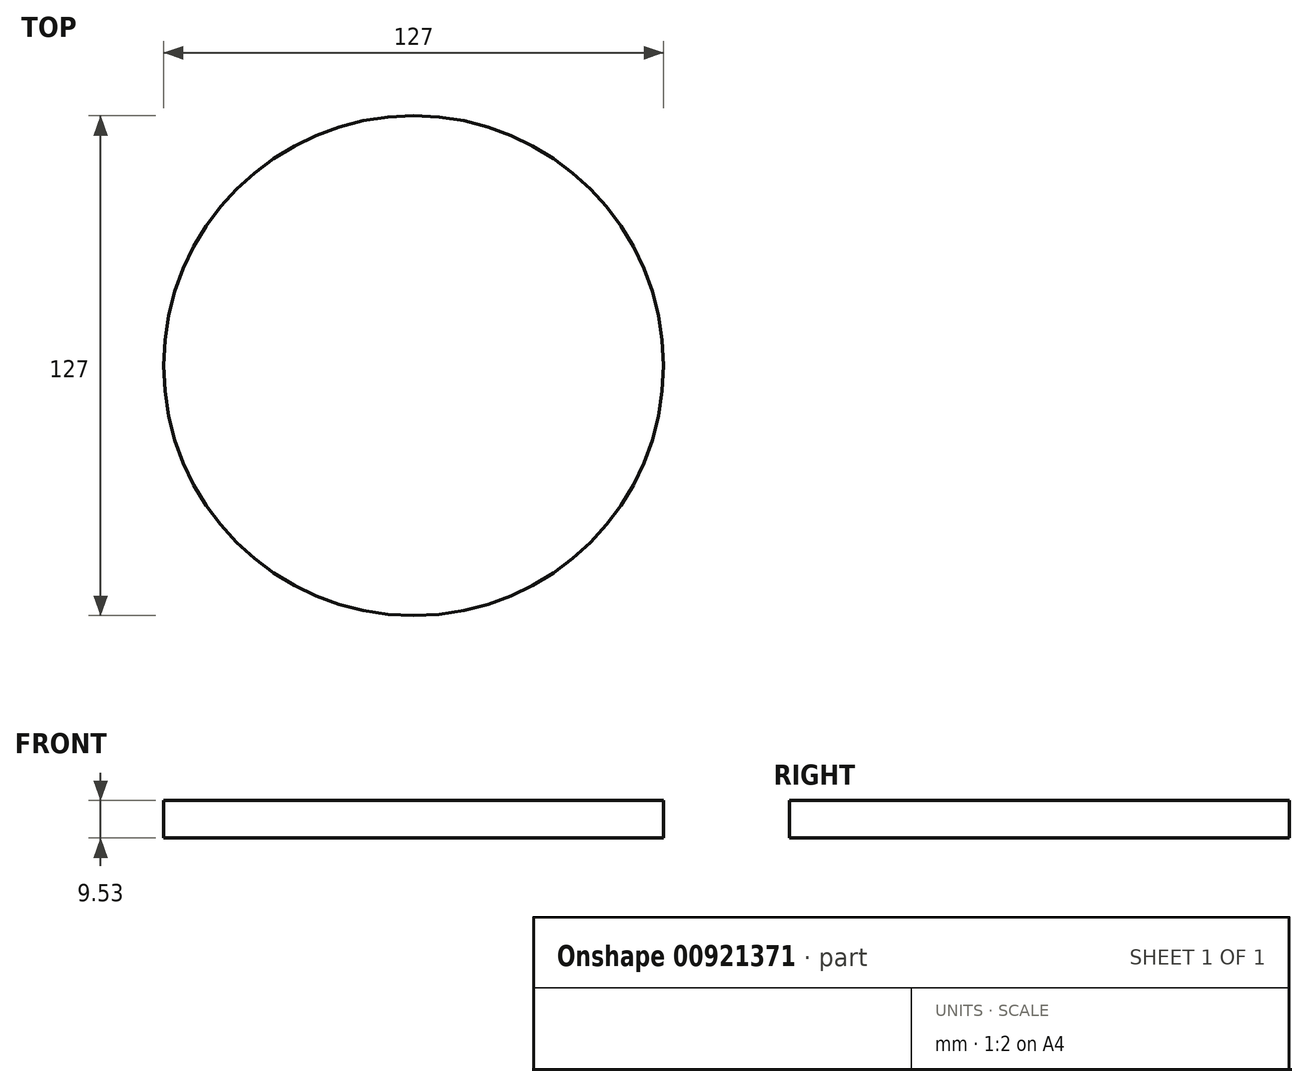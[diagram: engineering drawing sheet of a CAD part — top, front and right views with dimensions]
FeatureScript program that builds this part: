
annotation { "Feature Type Name" : "Feature", "Feature Type Description" : "" }
export const myFeature = defineFeature(function(context is Context, id is Id, definition is map)
    precondition{}
    {
        {
            var Q0;
            Q0=qCreatedBy(makeId("Top.planeOp"),FACE);
            var sketch = newSketch(context, id + "F0", { "sketchPlane" : qUnion([Q0])});
            skCircle(sketch, "E0", {"center": v(0, 0) * mm, "radius": 63.5 * mm});
            skSolve(sketch);
        }
        {
            var Q0;
            Q0 = qSketchRegion(id + "F0", true);
            extrude(context, id + "F1", {"entities" : qUnion([Q0]), "oppositeDirection" : true, "depth" : 9.52 * mm, "offsetDistance" : 25.4 * mm});
        }
    });
